# Revit family: KB200
name_source: partatom
category: Equipement spécialisé
revit_build: Autodesk Revit 2016 (Build: 20150220_1215(x64)
units: mm (PartAtom-declared; Revit-internal decimal feet)

## family parameters
Cote de connecteur circulaire = Utiliser le diamètre
Couper avec des vides une fois chargée = Non
Hôte = Face
Numéro OmniClass = 23.40.20.21
Partagée = Non
Point de calcul de pièce = Non
Titre OmniClass = Toilet and Bath Specialties
Type d'élément = Normal

## types (6) — shared parameters
Capacity = 200 lbs  ;  50 liners
Code d'assemblage = E1090900
Elévation par défaut = 0' - 0"
Fabricant = Bobrick Washroom Equipment, Inc.
Note d'identification = 102813
Recycled Content = 16%
Revision = R1_10_2012
Standards Conformance = ADA with proper mounting height  ;  Made in U.S.A.
URL = http://www.bobrick.com
Unit Depth = 0' - 3 3/4"
Unit Height = 1' - 10 1/4"
Unit Width = 2' - 11 3/16"
zero-valued in all types: Expected Lifespan (Years), Maintenance Schedule (Months), Warranty Duration (Years)

## per-type parameters (varying)
| type | Center Plate Finish | Cover Finish | Description | Fixture Material | Modèle | Sales Information | Send Message |
| White Granite with Stainless Cover | Steel - Bobrick - Stainless Satin | Plastic - Bobrick - White Granite | Bobrick Horizontal Baby Changing Station - Koala Kare KB200-05SS | Plastic - Bobrick - White Granite | KB200-05SS | https://www.anox.fr | https://www.anox.fr |
| Grey with Stainless Cover | Steel - Bobrick - Stainless Satin | Plastic - Bobrick - Grey | Bobrick Horizontal Baby Changing Station - Koala Kare KB200-01SS | Plastic - Bobrick - Grey | KB200-01SS | http://www.bobrick.com | http://www.arcat.com |
| Earth | Plastic - Bobrick - Earth | Plastic - Bobrick - Earth | Bobrick Horizontal Baby Changing Station - Koala Kare KB200-11 | Plastic - Bobrick - Earth | KB200-11 | http://www.bobrick.com | http://www.arcat.com |
| White Granite | Plastic - Bobrick - White Granite | Plastic - Bobrick - White Granite | Bobrick Horizontal Baby Changing Station - Koala Kare KB200-05 | Plastic - Bobrick - White Granite | KB200-05 | http://www.bobrick.com | http://www.arcat.com |
| Grey | Plastic - Bobrick - Grey | Plastic - Bobrick - Grey | Bobrick Horizontal Baby Changing Station - Koala Kare KB200-01 | Plastic - Bobrick - Grey | KB200-01 | http://www.bobrick.com | http://www.arcat.com |
| Cream | Plastic - Bobrick - Cream | Plastic - Bobrick - Cream | Bobrick Horizontal Baby Changing Station - Koala Kare KB200-00 | Plastic - Bobrick - Cream | KB200-00 | http://www.bobrick.com | http://www.arcat.com |

## geometry (parser evidence)
native form markers: Blend x6, Sweep x1
no freeform markers — native parametric forms only
